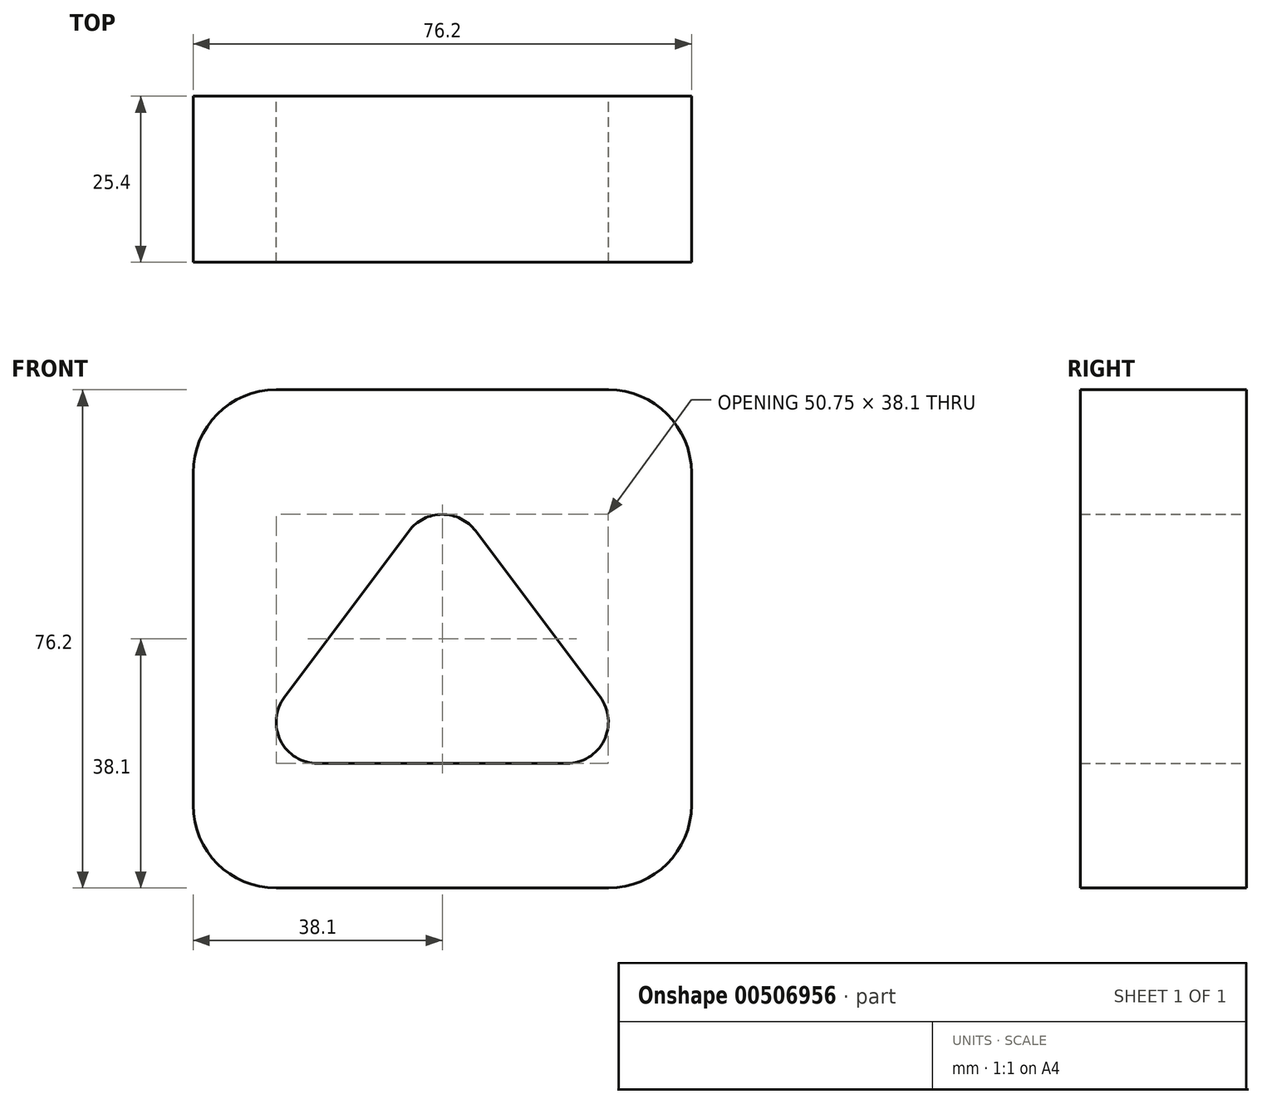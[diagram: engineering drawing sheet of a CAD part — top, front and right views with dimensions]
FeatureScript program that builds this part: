
annotation { "Feature Type Name" : "Feature", "Feature Type Description" : "" }
export const myFeature = defineFeature(function(context is Context, id is Id, definition is map)
    precondition{}
    {
        {
            var Q0;
            Q0=qCreatedBy(makeId("Front.planeOp"),FACE);
            var sketch = newSketch(context, id + "F0", { "sketchPlane" : qUnion([Q0])});
            skLineSegment(sketch, "E0", {"start": v(12.7, 0) * mm, "end": v(63.5, 0) * mm});
            skLineSegment(sketch, "E1", {"start": v(76.2, 12.7) * mm, "end": v(76.2, 63.5) * mm});
            skLineSegment(sketch, "E2", {"start": v(63.5, 76.2) * mm, "end": v(12.7, 76.2) * mm});
            skLineSegment(sketch, "E3", {"start": v(0, 63.5) * mm, "end": v(0, 12.7) * mm});
            skArc(sketch, "E4", {"start": v(13.97, 29.21) * mm, "mid": v(13.37, 22.56) * mm, "end": v(19.05, 19.05) * mm});
            skArc(sketch, "E5", {"start": v(57.15, 19.05) * mm, "mid": v(62.83, 22.56) * mm, "end": v(62.23, 29.21) * mm});
            skArc(sketch, "E6", {"start": v(43.18, 54.6) * mm, "mid": v(38.1, 57.15) * mm, "end": v(33.02, 54.6) * mm});
            skLineSegment(sketch, "E7", {"start": v(33.02, 54.6) * mm, "end": v(13.97, 29.21) * mm});
            skLineSegment(sketch, "E8", {"start": v(43.18, 54.6) * mm, "end": v(62.23, 29.21) * mm});
            skLineSegment(sketch, "E9", {"start": v(19.05, 19.05) * mm, "end": v(57.15, 19.05) * mm});
            skArc(sketch, "E10", {"start": v(12.7, 76.2) * mm, "mid": v(3.72, 72.48) * mm, "end": v(0, 63.5) * mm});
            skArc(sketch, "E11", {"start": v(76.2, 63.5) * mm, "mid": v(72.48, 72.48) * mm, "end": v(63.5, 76.2) * mm});
            skArc(sketch, "E12", {"start": v(0, 12.7) * mm, "mid": v(3.72, 3.72) * mm, "end": v(12.7, 0) * mm});
            skArc(sketch, "E13", {"start": v(63.5, 0) * mm, "mid": v(72.48, 3.72) * mm, "end": v(76.2, 12.7) * mm});
            skSolve(sketch);
        }
        {
            var Q0;
            Q0=makeQuery(id+"F0.imprint","IMPRINT",FACE,{"disambiguationData":[TD([[makeQuery(id+"F0.imprint","IMPRINT",EDGE,{"derivedFrom":sQuery(id+"F0.wireOp",EDGE,"E0")}),1.0]])]});
            extrude(context, id + "F1", {"entities" : qUnion([Q0]), "depth" : 25.4 * mm});
        }
    });
